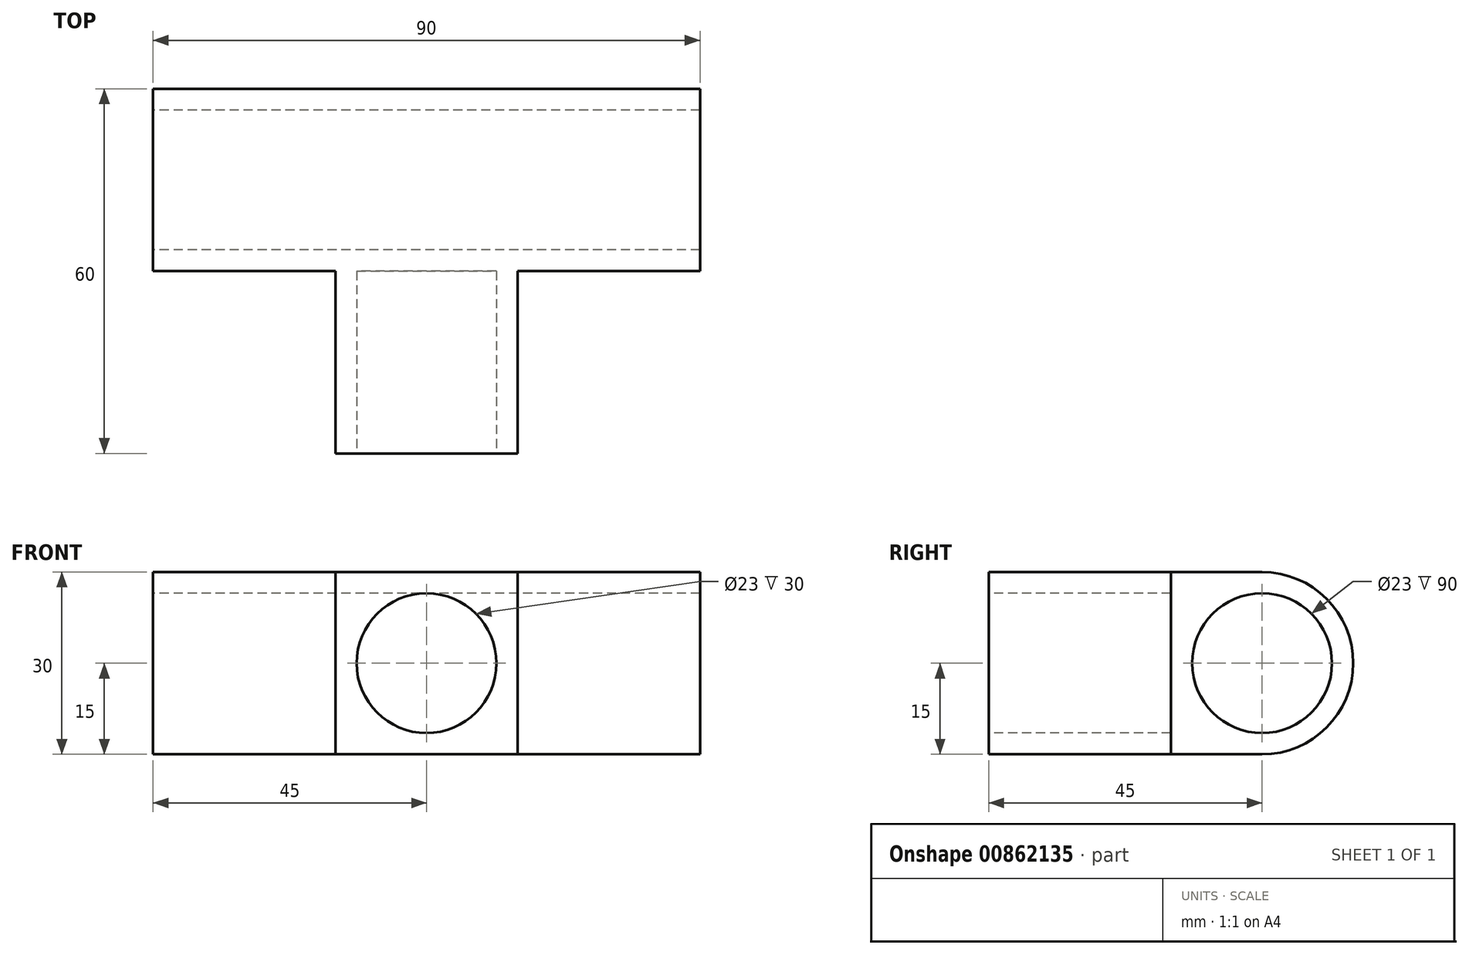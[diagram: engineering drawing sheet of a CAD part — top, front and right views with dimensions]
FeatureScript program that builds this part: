
annotation { "Feature Type Name" : "Feature", "Feature Type Description" : "" }
export const myFeature = defineFeature(function(context is Context, id is Id, definition is map)
    precondition{}
    {
        {
            var Q0;
            Q0=qCreatedBy(makeId("Top.planeOp"),FACE);
            var sketch = newSketch(context, id + "F0", { "sketchPlane" : qUnion([Q0])});
            skLineSegment(sketch, "E0.bottom", {"start": v(45, -15) * mm, "end": v(-45, -15) * mm});
            skLineSegment(sketch, "E0.top", {"start": v(45, 15) * mm, "end": v(-45, 15) * mm});
            skLineSegment(sketch, "E0.left", {"start": v(45, -15) * mm, "end": v(45, 15) * mm});
            skLineSegment(sketch, "E0.right", {"start": v(-45, -15) * mm, "end": v(-45, 15) * mm});
            skPoint(sketch, "E0.middle", {"position": v(0, 0) * mm});
            skLineSegment(sketch, "E1", {"start": v(-15, -15) * mm, "end": v(-15, -45) * mm});
            skLineSegment(sketch, "E2", {"start": v(-15, -45) * mm, "end": v(0, -45) * mm});
            skLineSegment(sketch, "E3.MirrorCS", {"start": v(15, -15) * mm, "end": v(15, -45) * mm});
            skLineSegment(sketch, "E4.MirrorCS", {"start": v(15, -45) * mm, "end": v(0, -45) * mm});
            skSolve(sketch);
        }
        {
            var Q0;
            Q0=makeQuery(id+"F0.imprint","IMPRINT",FACE,{"disambiguationData":[TD([[makeQuery(id+"F0.imprint","IMPRINT",EDGE,{"derivedFrom":sQuery(id+"F0.wireOp",EDGE,"E0.top")}),1.0]])]});
            var Q1;
            {var subQ1=sQuery(id+"F0.wireOp",EDGE,"E1");Q1=makeQuery(id+"F0.imprint","IMPRINT",FACE,{"disambiguationData":[TD([[makeQuery(id+"F0.imprint","IMPRINT",EDGE,{"derivedFrom":subQ1}),1.0]])]});}
            extrude(context, id + "F1", {"entities" : qUnion([Q0, Q1]), "depth" : 30 * mm, "offsetDistance" : 25 * mm});
        }
        {
            var Q0;
            Q0=makeQuery(id+"F1.opExtrude","SWEPT_FACE",FACE,{"disambiguationData":[OSD([sQuery(id+"F0.wireOp",EDGE,"E0.right")])]});
            var sketch = newSketch(context, id + "F2", { "sketchPlane" : qUnion([Q0])});
            skCircle(sketch, "E5", {"center": v(0, 15) * mm, "radius": 11.5 * mm});
            skPoint(sketch, "E5.centerSnap0", {"position": v(-15, 15) * mm});
            skPoint(sketch, "E5.centerSnap1", {"position": v(0, 30) * mm});
            skSolve(sketch);
        }
        {
            var Q0;
            Q0=makeQuery(id+"F1.opExtrude","SWEPT_FACE",FACE,{"disambiguationData":[OSD([sQuery(id+"F0.wireOp",EDGE,"E2"),sQuery(id+"F0.wireOp",EDGE,"E4.MirrorCS")])]});
            var sketch = newSketch(context, id + "F3", { "sketchPlane" : qUnion([Q0])});
            skCircle(sketch, "E6", {"center": v(0, 15) * mm, "radius": 11.5 * mm});
            skPoint(sketch, "E6.centerSnap0", {"position": v(-15, 15) * mm});
            skPoint(sketch, "E6.centerSnap1", {"position": v(0, 30) * mm});
            skSolve(sketch);
        }
        {
            var Q0;
            Q0=makeQuery(id+"F3.imprint","IMPRINT",FACE,{"disambiguationData":[TD([[makeQuery(id+"F3.imprint","IMPRINT",EDGE,{"derivedFrom":sQuery(id+"F3.wireOp",EDGE,"E6")}),1.0]])]});
            extrude(context, id + "F4", {"entities" : qUnion([Q0]), "operationType" : NewBodyOperationType.REMOVE, "oppositeDirection" : true, "depth" : 30 * mm, "offsetDistance" : 25 * mm});
        }
        {
            var Q0;
            Q0=makeQuery(id+"F2.imprint","IMPRINT",FACE,{"disambiguationData":[TD([[makeQuery(id+"F2.imprint","IMPRINT",EDGE,{"derivedFrom":sQuery(id+"F2.wireOp",EDGE,"E5")}),1.0]])]});
            extrude(context, id + "F5", {"entities" : qUnion([Q0]), "operationType" : NewBodyOperationType.REMOVE, "oppositeDirection" : true, "depth" : 90 * mm, "offsetDistance" : 25 * mm});
        }
        {
            var Q0;
            Q0=makeQuery(id+"F1.opExtrude","CAP_EDGE",EDGE,{"disambiguationData":[OSD([sQuery(id+"F0.wireOp",EDGE,"E0.top")])],"isStart":true});
            var Q1;
            Q1=makeQuery(id+"F1.opExtrude","CAP_EDGE",EDGE,{"disambiguationData":[OSD([sQuery(id+"F0.wireOp",EDGE,"E0.top")])],"isStart":false});
            fillet(context, id + "F6", {"entities" : qUnion([Q0, Q1]), "radius" : 15 * mm, "tangentPropagation" : true, "allowEdgeOverflow" : false});
        }
    });
